# Revit family: IS_ConnectSpace_E0392_BIM_DE
name_source: partatom
category: Plumbing Fixtures
revit_build: Autodesk Revit MEP 2016 (Build: 20161004_0715(x64)
units: mm (PartAtom-declared; Revit-internal decimal feet)

## family parameters
Always vertical = No
Cut with Voids When Loaded = No
OmniClass Number = 23.45.05.14.21.11
OmniClass Title = Bath/Shower Units
Part Type = Normal
Room Calculation Point = No
Round Connector Dimension = Use Diameter
Shared = No
Work Plane-Based = No

## types (3) — shared parameters
Accessories = www.idealstandard.de\ersatzteile
AssetType = Fixed
BIMobject category = Storage
BOSUseNativeGeometries = 1
Brand url = http://www.idealstandard.de
ConnectionType = Plumbing
CurrencyUnit = €
CurrentRevision = 1
DurationUnit = Jaar
EAN code = https://5017830455653
Edition number = 1
IFC Classification = Sanitary Terminal
IfcExportAs = Sanitary terminal type
Installation instructions = http://www.idealstandard.de
LinearUnits = millimetres
MaintenanceInformation = www.idealstandard.de
Manufacturer = http://www.idealstandard.de
Manufacturer name = Ideal Standard
ManufacturerURL = http://www.idealstandard.de
Material main = Glass
Nominal height = 6
Nominal width = 318
NominalHeight = 6 mm  [stored 0.019685 ft]
NominalLength = 232 mm  [stored 0.761155 ft]
NominalWidth = 318 mm  [stored 1.04331 ft]
Product Guid = 5a7a4488-fd60-45b5-88e6-6d7235ce8c32
Product SKU = E0392
Product data url = https://bimobject.com
Product family = CONNECT SPACE
Product group = Furniture
Product name = CONNECT SPACE glass shelf 218x232mm
Product url = http://www.idealstandard.de
ProductInformation = www.idealstandard.de/produkte
QR code = http://bimobject.com
Size = 318x232x6 mm
Space = Internal
SpareParts = www.idealstandard.de/ersatzteile
Technical description = http://www.idealstandard.de
URL = http://www.idealstandard.de
Uniclass2015Code = Pr_40_30_78_03
Uniclass2015Title = Bathroom cabinets
Uniclass2015Version = Products v1.1
VolumeUnits = Litres
Weight Net (Kg) = 1.1
zero-valued in all types: Cost

## per-type parameters (varying)
| type | BIMObjectName | Model | Name |
| E0392RP CONNECT SPACE glass shelf 218x232mm | ISI_IdealStandard_BathroomCabinets__E0393RP | E0393RP | ISI_IdealStandard_BathroomCabinets__E0393RP |
| E0392RU CONNECT SPACE glass shelf 218x232mm | ISI_IdealStandard_BathroomCabinets__E0393RU | E0393RU | ISI_IdealStandard_BathroomCabinets__E0393RU |
| E0392SA CONNECT SPACE glass shelf 218x232mm | ISI_IdealStandard_BathroomCabinets__E0393SA | E0393SA | ISI_IdealStandard_BathroomCabinets__E0393SA |

note: [stored X ft] marks values corroborated as IEEE doubles in the binary element streams (Revit-internal decimal feet)

## geometry (parser evidence)
native form markers: Blend x2, Sweep x2
no freeform markers — native parametric forms only
